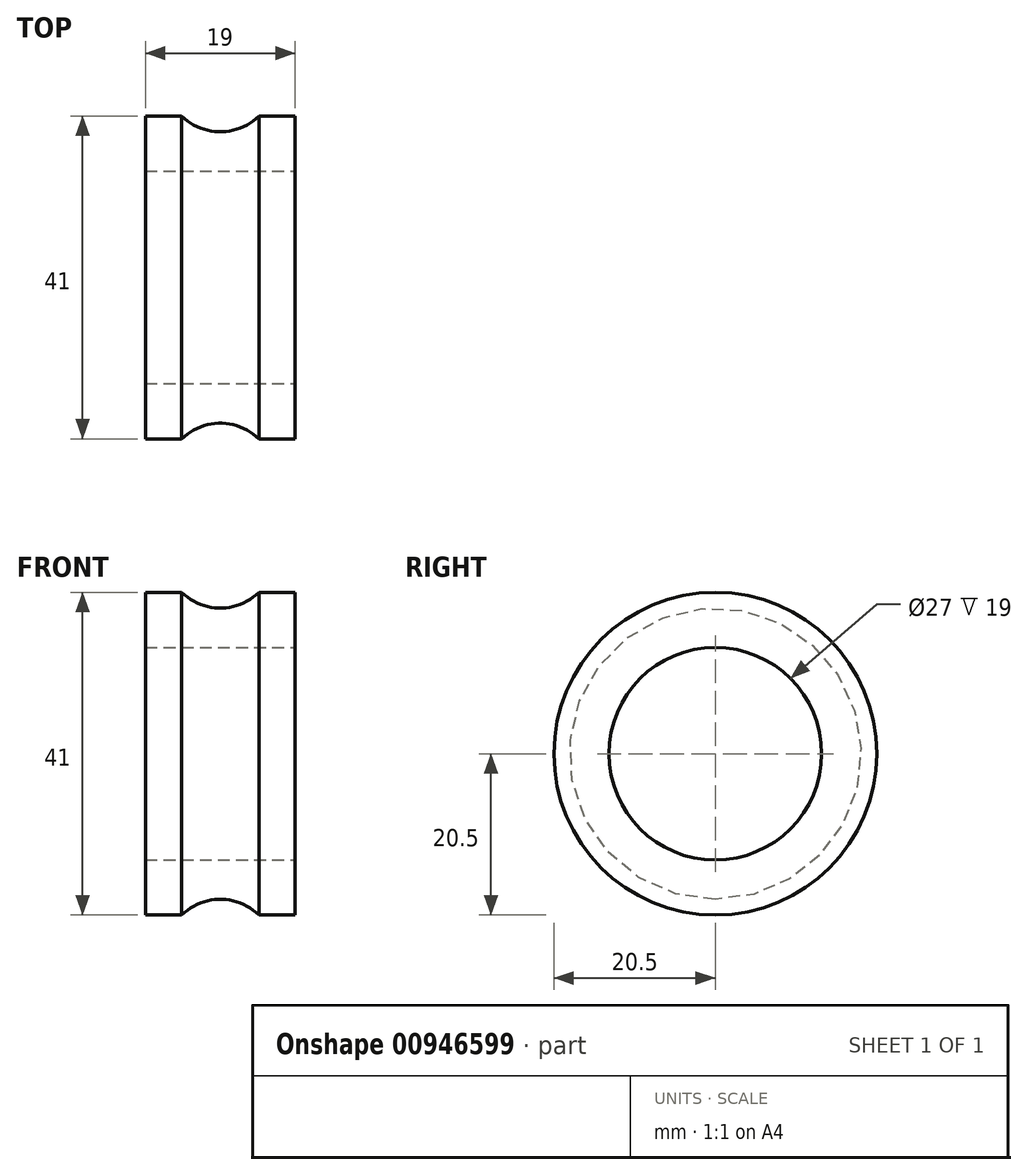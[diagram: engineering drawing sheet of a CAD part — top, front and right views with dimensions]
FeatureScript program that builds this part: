
annotation { "Feature Type Name" : "Feature", "Feature Type Description" : "" }
export const myFeature = defineFeature(function(context is Context, id is Id, definition is map)
    precondition{}
    {
        {
            var Q0;
            Q0=qCreatedBy(makeId("Front.planeOp"),FACE);
            var sketch = newSketch(context, id + "F0", { "sketchPlane" : qUnion([Q0])});
            skLineSegment(sketch, "E0.bottom", {"start": v(-9.5, 0) * mm, "end": v(9.5, 0) * mm});
            skLineSegment(sketch, "E0.top", {"start": v(-9.5, 7) * mm, "end": v(-4.9, 7) * mm});
            skLineSegment(sketch, "E0.left", {"start": v(-9.5, 0) * mm, "end": v(-9.5, 7) * mm});
            skLineSegment(sketch, "E0.right", {"start": v(9.5, 0) * mm, "end": v(9.5, 7) * mm});
            skArc(sketch, "E1", {"start": v(-4.9, 7) * mm, "mid": v(0, 5) * mm, "end": v(4.9, 7) * mm});
            skPoint(sketch, "E1.centerSnap0", {"position": v(0, 7) * mm});
            skLineSegment(sketch, "E2.trimOffspring", {"start": v(4.9, 7) * mm, "end": v(9.5, 7) * mm});
            skLineSegment(sketch, "E3", {"start": v(0, -13.5) * mm, "end": v(-17.08, -13.5) * mm, "construction": true});
            skLineSegment(sketch, "E4.MirrorCS", {"start": v(0, -13.5) * mm, "end": v(17.08, -13.5) * mm, "construction": true});
            skSolve(sketch);
        }
        {
            var Q0;
            Q0 = qSketchRegion(id + "F0", true);
            var Q1;
            Q1=sQuery(id+"F0.wireOp",EDGE,"E3");
            revolve(context, id + "F1", {"surfaceOperationType" : NewSurfaceOperationType.NEW, "entities" : qUnion([Q0]), "axis" : qUnion([Q1]), "revolveType" : RevolveType.FULL});
        }
    });
